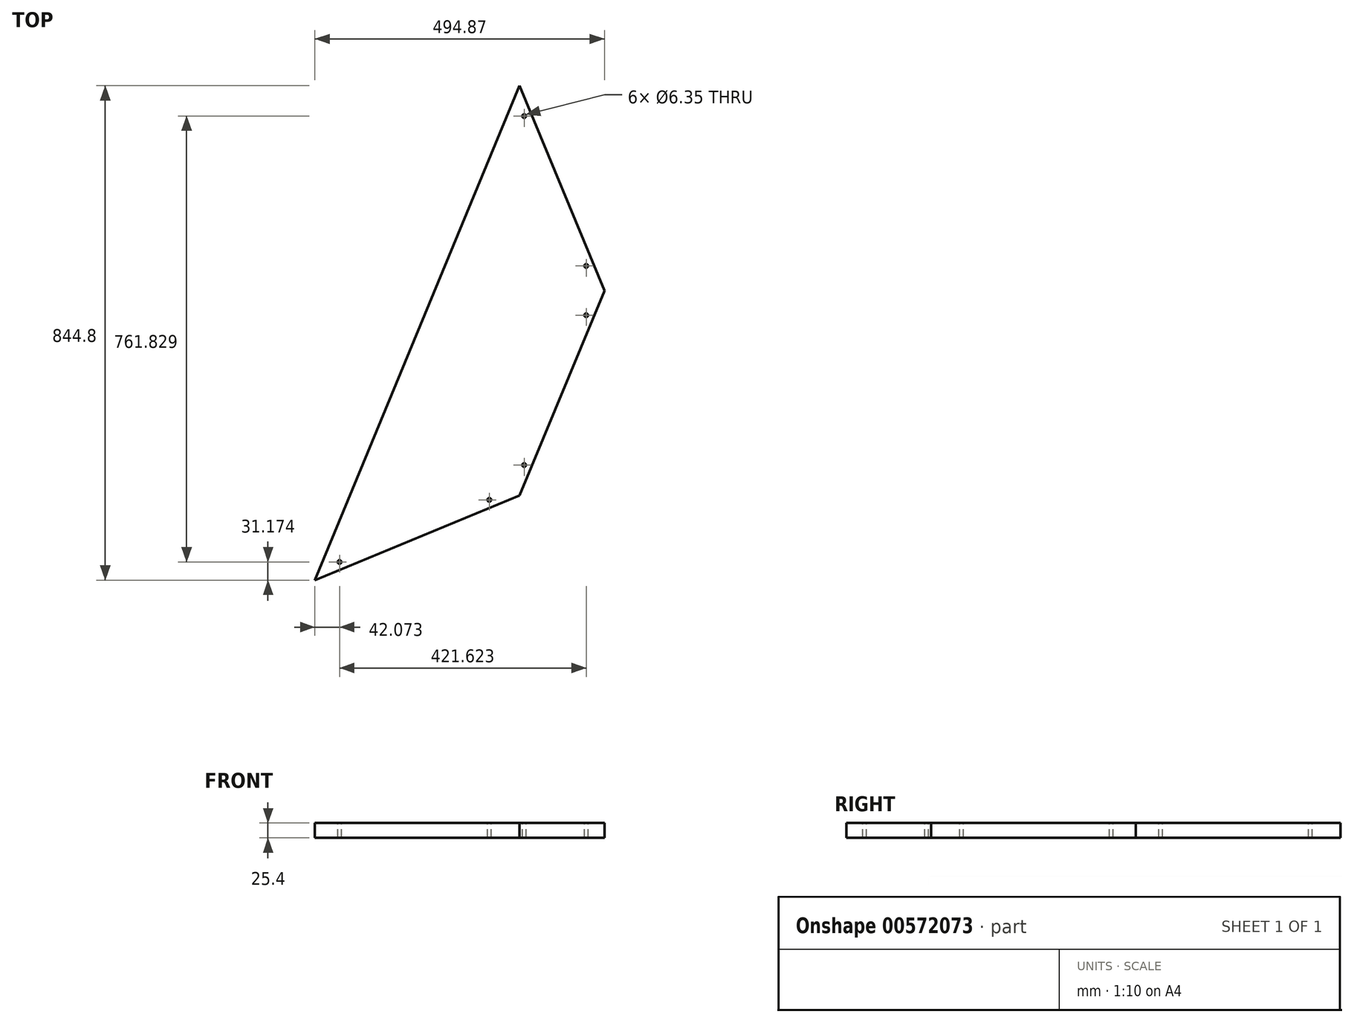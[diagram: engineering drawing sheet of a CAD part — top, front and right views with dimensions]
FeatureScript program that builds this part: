
annotation { "Feature Type Name" : "Feature", "Feature Type Description" : "" }
export const myFeature = defineFeature(function(context is Context, id is Id, definition is map)
    precondition{}
    {
        {
            var Q0;
            Q0=qCreatedBy(makeId("Top.planeOp"),FACE);
            var sketch = newSketch(context, id + "F0", { "sketchPlane" : qUnion([Q0])});
            skCircle(sketch, "E0.cCircle", {"center": v(0, 0) * mm, "radius": 494.87 * mm, "construction": true});
            skLineSegment(sketch, "E0.0", {"start": v(494.87, 0) * mm, "end": v(349.93, -349.93) * mm});
            skLineSegment(sketch, "E0.1", {"start": v(349.93, -349.93) * mm, "end": v(0, -494.87) * mm});
            skLineSegment(sketch, "E0.2", {"start": v(0, -494.87) * mm, "end": v(-349.93, -349.93) * mm});
            skLineSegment(sketch, "E0.3", {"start": v(-349.93, -349.93) * mm, "end": v(-494.87, 0) * mm});
            skLineSegment(sketch, "E0.4", {"start": v(-494.87, 0) * mm, "end": v(-349.93, 349.93) * mm});
            skLineSegment(sketch, "E0.5", {"start": v(-349.93, 349.93) * mm, "end": v(0, 494.87) * mm});
            skLineSegment(sketch, "E0.6", {"start": v(0, 494.87) * mm, "end": v(349.93, 349.93) * mm});
            skLineSegment(sketch, "E0.7", {"start": v(349.93, 349.93) * mm, "end": v(494.87, 0) * mm});
            skLineSegment(sketch, "E1", {"start": v(349.93, 349.93) * mm, "end": v(0, -494.87) * mm});
            skSolve(sketch);
        }
        {
            var Q0;
            Q0=makeQuery(id+"F0.imprint","IMPRINT",FACE,{"disambiguationData":[TD([[makeQuery(id+"F0.imprint","IMPRINT",EDGE,{"derivedFrom":sQuery(id+"F0.wireOp",EDGE,"E0.0")}),-1.0]])]});
            extrude(context, id + "F1", {"entities" : qUnion([Q0]), "depth" : 25.4 * mm, "offsetDistance" : 25.4 * mm});
        }
        {
            var Q0;
            Q0=makeQuery(id+"F1.opExtrude","CAP_FACE",FACE,{"disambiguationData":[OSD([sQuery(id+"F0.wireOp",EDGE,"E0.0"),sQuery(id+"F0.wireOp",EDGE,"E0.1"),sQuery(id+"F0.wireOp",EDGE,"E0.7"),sQuery(id+"F0.wireOp",EDGE,"E1")])],"isStart":false});
            var sketch = newSketch(context, id + "F2", { "sketchPlane" : qUnion([Q0])});
            skCircle(sketch, "E2", {"center": v(42.07, -463.7) * mm, "radius": 3.18 * mm});
            skCircle(sketch, "E3", {"center": v(298.13, -357.63) * mm, "radius": 3.17 * mm});
            skCircle(sketch, "E4", {"center": v(357.63, -298.13) * mm, "radius": 3.17 * mm});
            skCircle(sketch, "E5", {"center": v(463.7, -42.07) * mm, "radius": 3.17 * mm});
            skCircle(sketch, "E6", {"center": v(463.7, 42.07) * mm, "radius": 3.17 * mm});
            skCircle(sketch, "E7", {"center": v(357.63, 298.13) * mm, "radius": 3.18 * mm});
            skLineSegment(sketch, "E8", {"start": v(357.63, 298.13) * mm, "end": v(360.57, 299.35) * mm});
            skLineSegment(sketch, "E9", {"start": v(360.57, 299.35) * mm, "end": v(369.37, 303) * mm});
            skLineSegment(sketch, "E10", {"start": v(463.7, 42.07) * mm, "end": v(466.63, 43.29) * mm});
            skLineSegment(sketch, "E11", {"start": v(466.63, 43.29) * mm, "end": v(475.43, 46.93) * mm});
            skLineSegment(sketch, "E12", {"start": v(463.7, -42.07) * mm, "end": v(460.76, -40.86) * mm});
            skLineSegment(sketch, "E13", {"start": v(298.13, -357.63) * mm, "end": v(299.35, -360.57) * mm});
            skLineSegment(sketch, "E14", {"start": v(299.35, -360.57) * mm, "end": v(303, -369.37) * mm});
            skLineSegment(sketch, "E15", {"start": v(42.07, -463.7) * mm, "end": v(43.29, -466.63) * mm});
            skLineSegment(sketch, "E16", {"start": v(43.29, -466.63) * mm, "end": v(46.93, -475.43) * mm});
            skLineSegment(sketch, "E17", {"start": v(357.63, -298.13) * mm, "end": v(354.7, -296.92) * mm});
            skLineSegment(sketch, "E18", {"start": v(354.7, -296.92) * mm, "end": v(369.37, -303) * mm});
            skLineSegment(sketch, "E19", {"start": v(463.7, -42.07) * mm, "end": v(475.43, -46.93) * mm});
            skSolve(sketch);
        }
        {
            var Q0;
            Q0=qSketchRegion(id+"F2",true);
            extrude(context, id + "F3", {"entities" : qUnion([Q0]), "operationType" : NewBodyOperationType.REMOVE, "endBound" : BoundingType.THROUGH_ALL, "oppositeDirection" : true, "depth" : 25.4 * mm, "offsetDistance" : 25.4 * mm});
        }
    });
